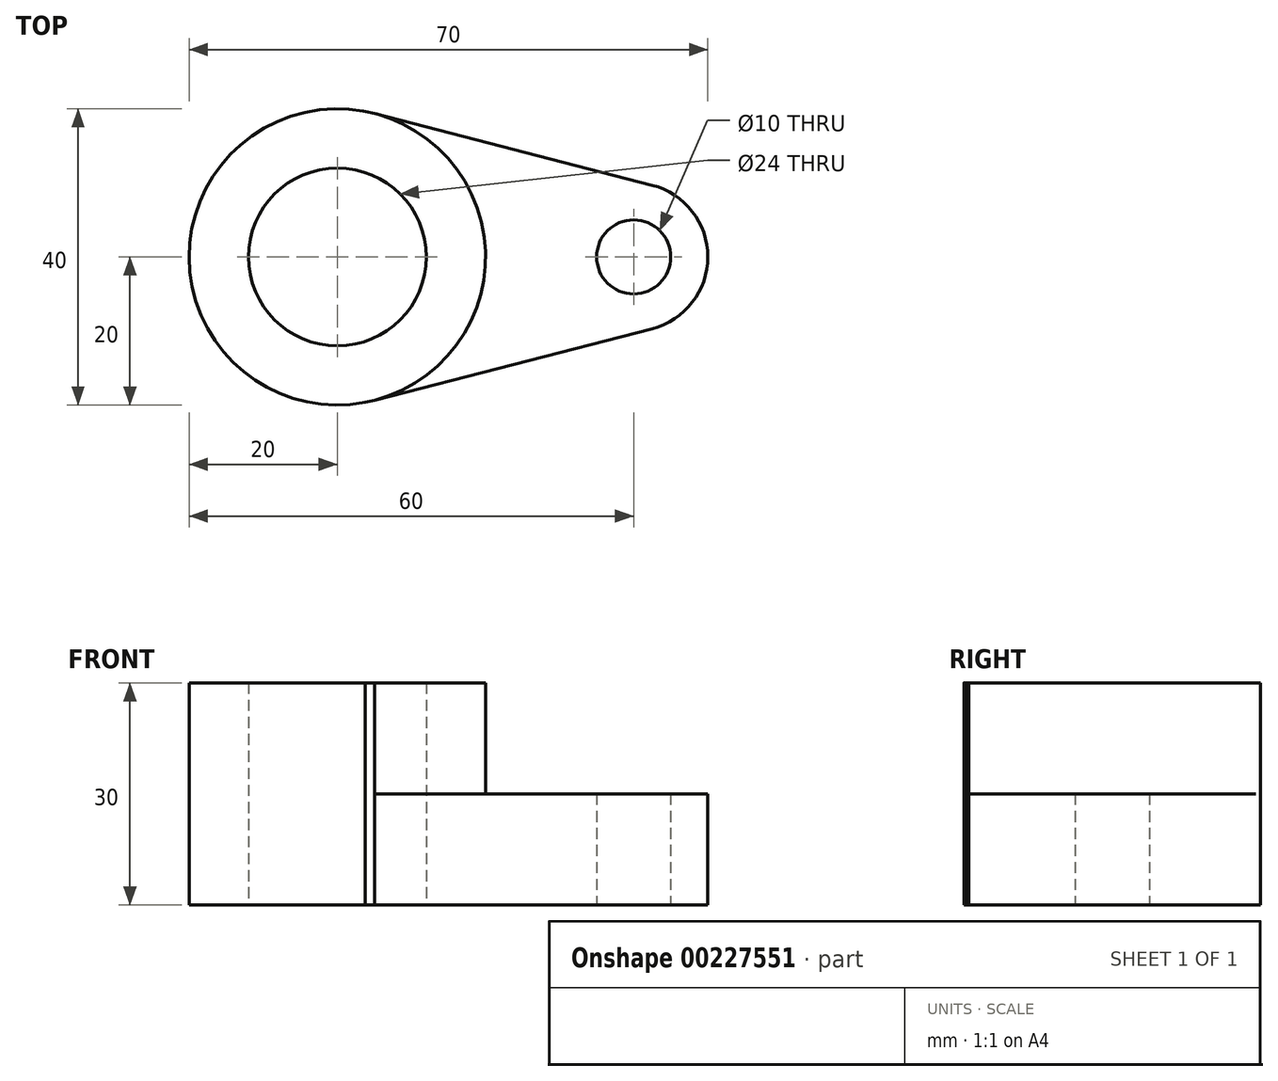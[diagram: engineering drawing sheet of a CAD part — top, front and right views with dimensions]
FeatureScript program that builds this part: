
annotation { "Feature Type Name" : "Feature", "Feature Type Description" : "" }
export const myFeature = defineFeature(function(context is Context, id is Id, definition is map)
    precondition{}
    {
        {
            var Q0;
            Q0=qCreatedBy(makeId("Top.planeOp"),FACE);
            var sketch = newSketch(context, id + "F0", { "sketchPlane" : qUnion([Q0])});
            skCircle(sketch, "E0", {"center": v(0, 0) * mm, "radius": 12 * mm});
            skCircle(sketch, "E1", {"center": v(0, 0) * mm, "radius": 20 * mm});
            skCircle(sketch, "E2", {"center": v(40, 0) * mm, "radius": 5 * mm});
            skArc(sketch, "E3", {"start": v(42.5, -9.68) * mm, "mid": v(50, 0) * mm, "end": v(42.5, 9.68) * mm});
            skLineSegment(sketch, "E4", {"start": v(5, 19.36) * mm, "end": v(42.5, 9.68) * mm});
            skLineSegment(sketch, "E5", {"start": v(5, -19.36) * mm, "end": v(3.74, -19.65) * mm});
            skLineSegment(sketch, "E6", {"start": v(5, -19.36) * mm, "end": v(42.5, -9.68) * mm});
            skSolve(sketch);
        }
        {
            var Q0;
            Q0=makeQuery(id+"F0.imprint","IMPRINT",FACE,{"disambiguationData":[TD([[makeQuery(id+"F0.imprint","IMPRINT",EDGE,{"derivedFrom":sQuery(id+"F0.wireOp",EDGE,"E2")}),-1.0]])]});
            extrude(context, id + "F1", {"entities" : qUnion([Q0]), "depth" : 15 * mm});
        }
        {
            var Q0;
            Q0=makeQuery(id+"F0.imprint","IMPRINT",FACE,{"disambiguationData":[TD([[makeQuery(id+"F0.imprint","IMPRINT",EDGE,{"derivedFrom":sQuery(id+"F0.wireOp",EDGE,"E0")}),-1.0]])]});
            extrude(context, id + "F2", {"entities" : qUnion([Q0]), "operationType" : NewBodyOperationType.ADD, "depth" : 30 * mm});
        }
    });
